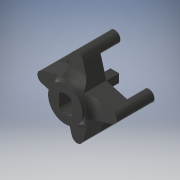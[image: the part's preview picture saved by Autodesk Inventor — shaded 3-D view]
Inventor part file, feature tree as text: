
AUTODESK INVENTOR PART (.ipt)
format: ipt  version: 2019 (Build 230136000, 136)  size: 208,896 bytes
history: native  units: in
note: dims shown in document units (in); Inventor stores cm internally (conversion verified against a paired STEP export)
features: extrude x5, fillet x3, sketch x2, pattern_circular x1, move_body x1
ambient origin geometry x8: Origin, YZ Plane, XZ Plane, XY Plane, X Axis, Y Axis, Z Axis, Center Point
bodies: Solid1 (feature_tree)
feature tree (12):
  sketch  "Sketch1"  dims[d0=0.275in d1=0.0946in]
  extrude  "Extrusion1"  Depth=0.0946in
  sketch  "Sketch2"  dims[d2=0.5in d3=0.0591in d4=0.425in d5=0.0in d6=0.315in d7=0.5in d8=0.25in d9=0.1969in d10=0.1614in d15=0.122in d27=0.25in d28=0.0in d29=1.5748in d30=360.0deg d32=0.3in d33=0.0in d34=0.3in d35=0.0in d42=0.25in d43=0.0in d44=0.125in d45=0.125in d46=0.0625in d53=180.0deg]
  extrude  "Extrusion2"  Depth=0.125in
  extrude  "Extrusion3"  Depth=0.125in TaperAngle=0.0deg
  extrude  "Extrusion4"  Depth=0.125in
  pattern_circular  "Circular Pattern1"  [2 undecoded]
  extrude  "Extrusion5"  Depth=0.125in
  fillet  "Fillet1"  Radius=0.1969in
  fillet  "Fillet2"  Radius=0.1614in
  fillet  "Fillet3"  Radius=0.122in
  move_body  "Move Body1"
note: 2 required parameter values undecoded (feature->parameter linkage not recoverable at this tier; creation-order binding heuristic only, values carry confidence <= 0.55)
